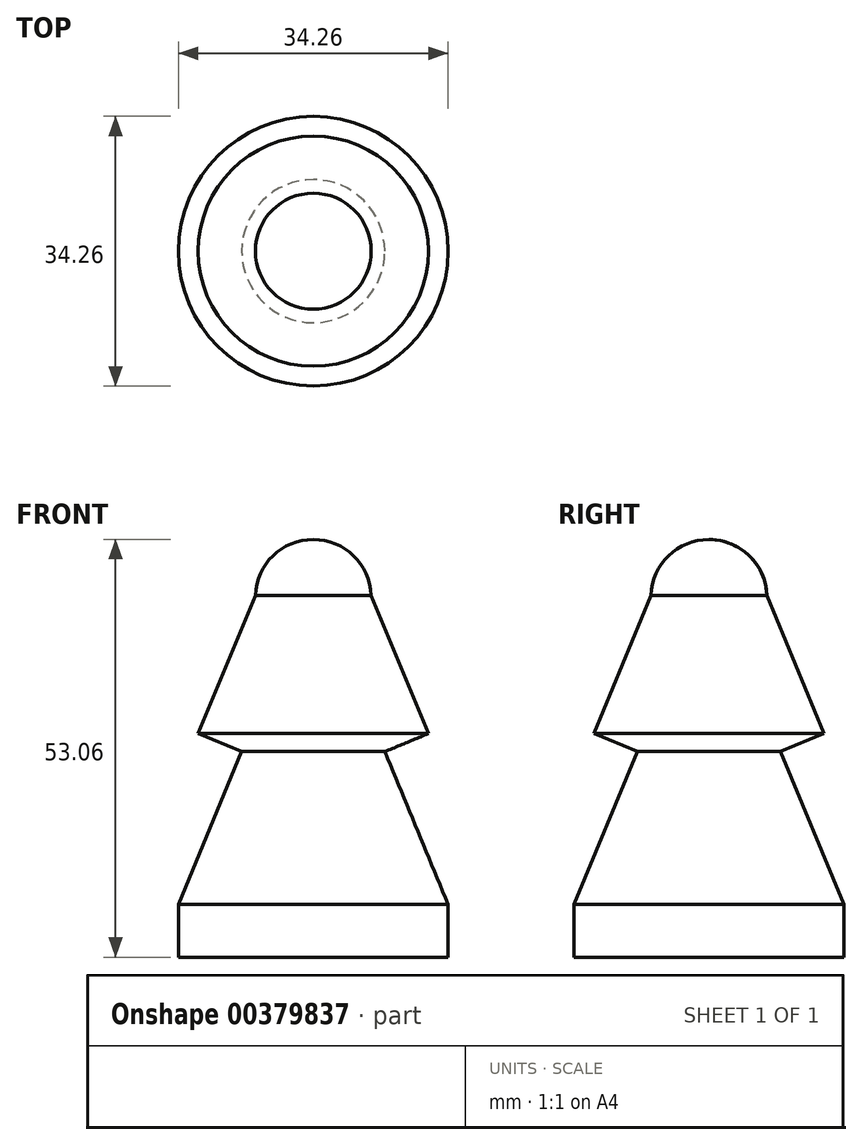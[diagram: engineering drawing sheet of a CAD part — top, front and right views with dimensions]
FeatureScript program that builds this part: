
annotation { "Feature Type Name" : "Feature", "Feature Type Description" : "" }
export const myFeature = defineFeature(function(context is Context, id is Id, definition is map)
    precondition{}
    {
        {
            var Q0;
            Q0=qCreatedBy(makeId("Right.planeOp"),FACE);
            var sketch = newSketch(context, id + "F0", { "sketchPlane" : qUnion([Q0])});
            skLineSegment(sketch, "E0", {"start": v(0, 44.07) * mm, "end": v(0, -18.38) * mm, "construction": true});
            skArc(sketch, "E1", {"start": v(7.36, 33) * mm, "mid": v(5.11, 38.04) * mm, "end": v(0, 40.1) * mm});
            skLineSegment(sketch, "E2", {"start": v(7.36, 33) * mm, "end": v(14.62, 15.46) * mm});
            skLineSegment(sketch, "E3", {"start": v(14.62, 15.46) * mm, "end": v(9.09, 13.17) * mm});
            skLineSegment(sketch, "E4", {"start": v(9.09, 13.17) * mm, "end": v(17.13, -6.27) * mm});
            skLineSegment(sketch, "E5", {"start": v(17.13, -6.27) * mm, "end": v(17.13, -12.95) * mm});
            skLineSegment(sketch, "E6", {"start": v(17.13, -12.95) * mm, "end": v(0, -12.95) * mm});
            skLineSegment(sketch, "E7", {"start": v(0, -12.95) * mm, "end": v(0, 40.1) * mm});
            skSolve(sketch);
        }
        {
            var Q0;
            Q0 = qSketchRegion(id + "F0", true);
            var Q1;
            Q1=sQuery(id+"F0.wireOp",EDGE,"E0");
            revolve(context, id + "F1", {"entities" : qUnion([Q0]), "axis" : qUnion([Q1]), "revolveType" : RevolveType.FULL});
        }
    });
